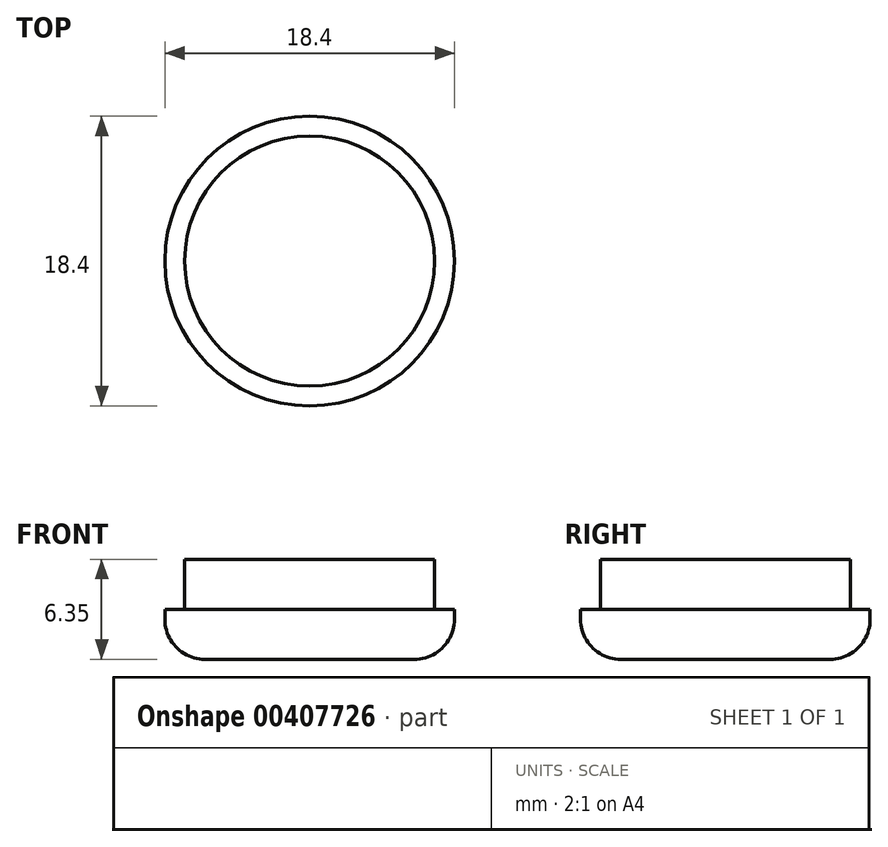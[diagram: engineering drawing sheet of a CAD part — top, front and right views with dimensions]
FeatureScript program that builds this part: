
annotation { "Feature Type Name" : "Feature", "Feature Type Description" : "" }
export const myFeature = defineFeature(function(context is Context, id is Id, definition is map)
    precondition{}
    {
        {
            var Q0;
            Q0=qCreatedBy(makeId("Top.planeOp"),FACE);
            var sketch = newSketch(context, id + "F0", { "sketchPlane" : qUnion([Q0])});
            skCircle(sketch, "E0", {"center": v(0, 0) * mm, "radius": 9.2 * mm});
            skCircle(sketch, "E1", {"center": v(0, 0) * mm, "radius": 7.94 * mm});
            skSolve(sketch);
        }
        {
            var Q0;
            Q0=makeQuery(id+"F0.imprint","IMPRINT",FACE,{"disambiguationData":[TD([[makeQuery(id+"F0.imprint","IMPRINT",EDGE,{"derivedFrom":sQuery(id+"F0.wireOp",EDGE,"E1")}),1.0]])]});
            extrude(context, id + "F1", {"entities" : qUnion([Q0]), "depth" : 6.35 * mm, "offsetDistance" : 25.4 * mm});
        }
        {
            var Q0;
            Q0=makeQuery(id+"F0.imprint","IMPRINT",FACE,{"disambiguationData":[TD([[makeQuery(id+"F0.imprint","IMPRINT",EDGE,{"derivedFrom":sQuery(id+"F0.wireOp",EDGE,"E0")}),1.0]])]});
            extrude(context, id + "F2", {"entities" : qUnion([Q0]), "operationType" : NewBodyOperationType.ADD, "depth" : 3.17 * mm, "offsetDistance" : 25.4 * mm});
        }
        {
            var Q0;
            Q0=makeQuery(id+"F2.opExtrude","CAP_EDGE",EDGE,{"disambiguationData":[OSD([sQuery(id+"F0.wireOp",EDGE,"E0")])],"isStart":true});
            fillet(context, id + "F3", {"entities" : qUnion([Q0]), "radius" : 2.54 * mm, "tangentPropagation" : true, "allowEdgeOverflow" : false});
        }
    });
